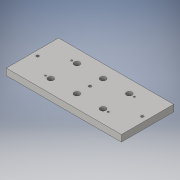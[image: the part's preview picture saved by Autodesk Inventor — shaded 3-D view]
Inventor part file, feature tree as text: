
AUTODESK INVENTOR PART (.ipt)
format: ipt  version: 2016 (Build 200138000, 138)  size: 140,288 bytes
history: native  units: mm
features: sketch x4, hole x3, projected_geometry x3, extrude x1
ambient origin geometry x8: Origin, YZ Plane, XZ Plane, XY Plane, X Axis, Y Axis, Z Axis, Center Point
bodies: Solid1 (feature_tree)
feature tree (11):
  extrude  "Extrusion1"  Depth=220.0mm
  hole  "Hole1"  [1 undecoded]
  hole  "Hole2"  [1 undecoded]
  hole  "Hole3"  [1 undecoded]
  sketch  "Sketch1"  dims[d0=100.0mm d1=220.0mm]
  sketch  "Sketch2"  dims[d2=110.0mm d3=12.5mm d4=0.0mm]
  projected_geometry  "Projected Loop1"
  sketch  "Sketch3"  dims[d5=50.0mm d6=120.0mm]
  projected_geometry  "Projected Loop2"
  sketch  "Sketch4"  dims[d7=3.242mm d8=8.0mm d9=4.0mm d10=2.0mm d11=90.0deg d12=11.8mm d13=20.594885mm d14=100.0mm d15=4.917mm d16=12.0mm d17=4.0mm d18=2.0mm d19=90.0deg d20=17.1mm d21=20.594885mm d22=50.0mm d23=25.0mm d24=30.0mm d26=50.0mm d27=20.0mm d29=50.0mm d32=6.0mm d33=12.0mm d34=10.5mm d35=7.0mm d36=90.0deg d37=17.1mm d38=20.594885mm d39=100.0mm]
  projected_geometry  "Projected Loop3"
note: 3 required parameter values undecoded (feature->parameter linkage not recoverable at this tier; creation-order binding heuristic only, values carry confidence <= 0.55)
